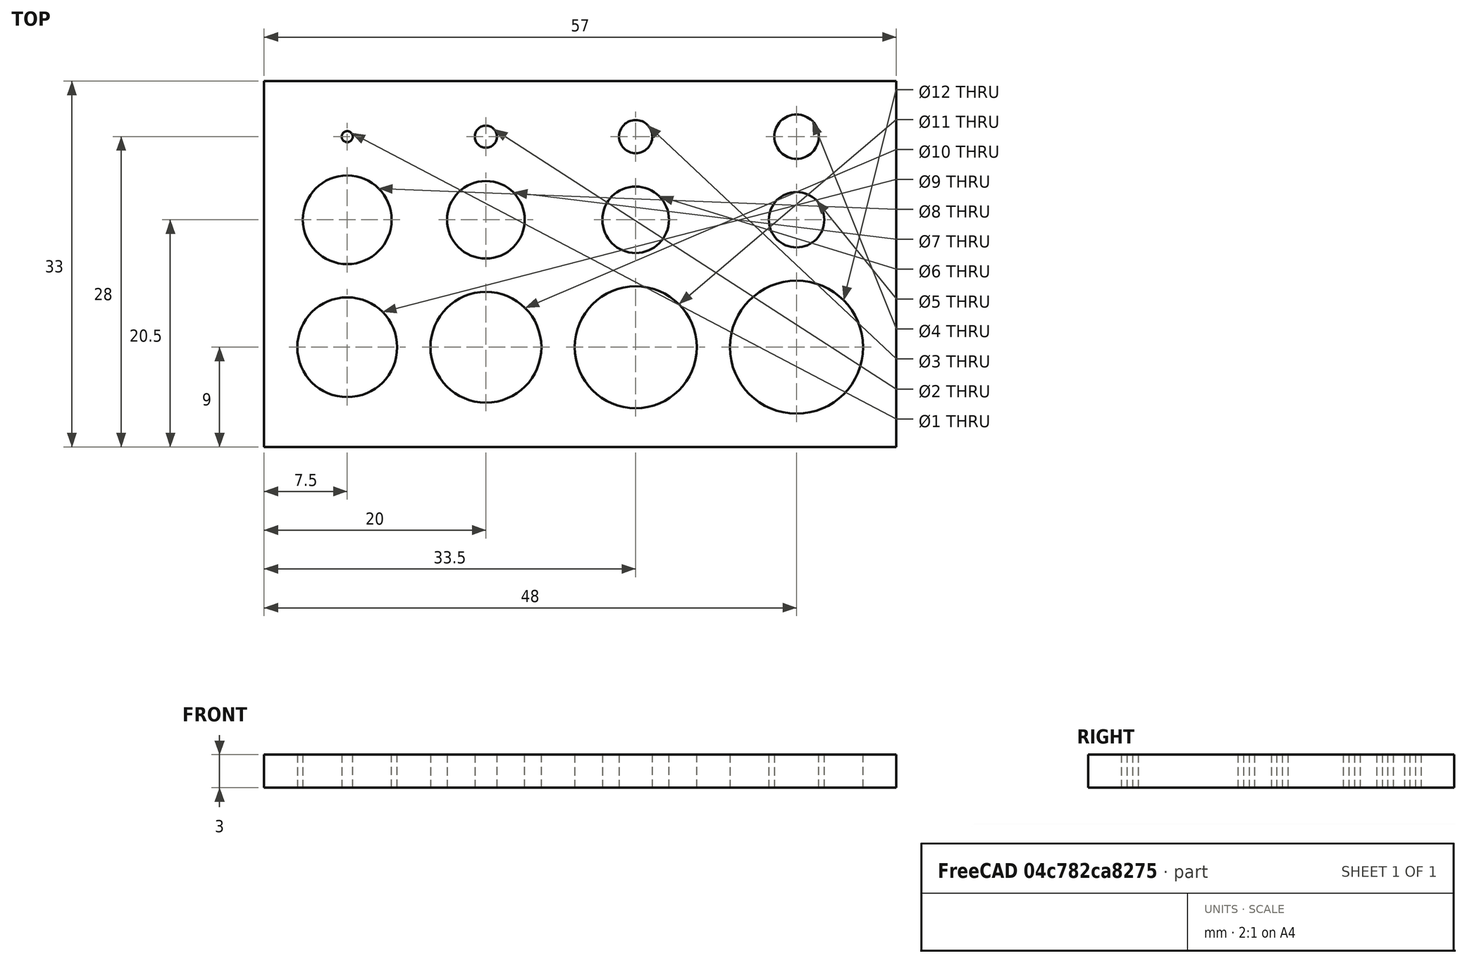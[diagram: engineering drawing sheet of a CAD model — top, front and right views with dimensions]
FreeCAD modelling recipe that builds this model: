
FCSTD DOCUMENT  (FreeCAD 0.14R3700 (Git))
Label: HolePattern
License: CC-BY 3.0
LicenseURL: http://creativecommons.org/licenses/by/3.0/
objects: Sketcher::SketchObject×1, PartDesign::Pad×1
note: 3 computed .brp shape members not serialized (recipe doc carries the construction recipe); baked Part::Feature solids carry a one-line shape summary decoded from their .brp

FEATURE [Sketcher::SketchObject] Sketch
  sketch-geometry (35):
    g0: LineSegment StartX=0 StartY=0 StartZ=0 EndX=57 EndY=0 EndZ=0
    g1: LineSegment StartX=57 StartY=0 StartZ=0 EndX=57 EndY=33 EndZ=0
    g2: LineSegment StartX=57 StartY=33 StartZ=0 EndX=0 EndY=33 EndZ=0
    g3: LineSegment StartX=0 StartY=33 StartZ=0 EndX=0 EndY=0 EndZ=0
    g4: LineSegment [constr] StartX=0 StartY=33 StartZ=0 EndX=0 EndY=28 EndZ=0
    g5: LineSegment [constr] StartX=0 StartY=28 StartZ=0 EndX=7.5 EndY=28 EndZ=0
    g6: LineSegment [constr] StartX=7.5 StartY=28 StartZ=0 EndX=20 EndY=28 EndZ=0
    g7: LineSegment [constr] StartX=20 StartY=28 StartZ=0 EndX=33.5 EndY=28 EndZ=0
    g8: LineSegment [constr] StartX=33.5 StartY=28 StartZ=0 EndX=48 EndY=28 EndZ=0
    g9: LineSegment [constr] StartX=48 StartY=28 StartZ=0 EndX=57 EndY=28 EndZ=0
    g10: LineSegment [constr] StartX=57 StartY=28 StartZ=0 EndX=57 EndY=20.5 EndZ=0
    g11: LineSegment [constr] StartX=57 StartY=20.5 StartZ=0 EndX=48 EndY=20.5 EndZ=0
    g12: LineSegment [constr] StartX=48 StartY=20.5 StartZ=0 EndX=33.5 EndY=20.5 EndZ=0
    g13: LineSegment [constr] StartX=33.5 StartY=20.5 StartZ=0 EndX=20 EndY=20.5 EndZ=0
    g14: LineSegment [constr] StartX=20 StartY=20.5 StartZ=0 EndX=7.5 EndY=20.5 EndZ=0
    g15: LineSegment [constr] StartX=7.5 StartY=20.5 StartZ=0 EndX=0 EndY=20.5 EndZ=0
    g16: LineSegment [constr] StartX=0 StartY=20.5 StartZ=0 EndX=0 EndY=9 EndZ=0
    g17: LineSegment [constr] StartX=0 StartY=9 StartZ=0 EndX=7.5 EndY=9 EndZ=0
    g18: LineSegment [constr] StartX=7.5 StartY=9 StartZ=0 EndX=20 EndY=9 EndZ=0
    g19: LineSegment [constr] StartX=20 StartY=9 StartZ=0 EndX=33.5 EndY=9 EndZ=0
    g20: LineSegment [constr] StartX=33.5 StartY=9 StartZ=0 EndX=48 EndY=9 EndZ=0
    g21: LineSegment [constr] StartX=48 StartY=9 StartZ=0 EndX=57 EndY=9 EndZ=0
    g22: LineSegment [constr] StartX=57 StartY=9 StartZ=0 EndX=57 EndY=0 EndZ=0
    g23: Circle CenterX=7.5 CenterY=28 CenterZ=0 NormalX=0 NormalY=0 NormalZ=1 Radius=0.5
    g24: Circle CenterX=20 CenterY=28 CenterZ=0 NormalX=0 NormalY=0 NormalZ=1 Radius=1
    g25: Circle CenterX=33.5 CenterY=28 CenterZ=0 NormalX=0 NormalY=0 NormalZ=1 Radius=1.5
    g26: Circle CenterX=48 CenterY=28 CenterZ=0 NormalX=0 NormalY=0 NormalZ=1 Radius=2
    g27: Circle CenterX=7.5 CenterY=20.5 CenterZ=0 NormalX=0 NormalY=0 NormalZ=1 Radius=4
    g28: Circle CenterX=20 CenterY=20.5 CenterZ=0 NormalX=0 NormalY=0 NormalZ=1 Radius=3.5
    g29: Circle CenterX=33.5 CenterY=20.5 CenterZ=0 NormalX=0 NormalY=0 NormalZ=1 Radius=3
    g30: Circle CenterX=48 CenterY=20.5 CenterZ=0 NormalX=0 NormalY=0 NormalZ=1 Radius=2.5
    g31: Circle CenterX=7.5 CenterY=9 CenterZ=0 NormalX=0 NormalY=0 NormalZ=1 Radius=4.5
    g32: Circle CenterX=20 CenterY=9 CenterZ=0 NormalX=0 NormalY=0 NormalZ=1 Radius=5
    g33: Circle CenterX=33.5 CenterY=9 CenterZ=0 NormalX=0 NormalY=0 NormalZ=1 Radius=5.5
    g34: Circle CenterX=48 CenterY=9 CenterZ=0 NormalX=0 NormalY=0 NormalZ=1 Radius=6
  constraints (91):
    c: Coincident(g0,g1)
    c: Coincident(g1,g2)
    c: Coincident(g2,g3)
    c: Coincident(g3,g0)
    c: Horizontal(g0)
    c: Horizontal(g2)
    c: Vertical(g1)
    c: Vertical(g3)
    c: Coincident(g0,g-1)
    c: Coincident(g2,g4)
    c: Coincident(g4,g5)
    c: Horizontal(g5)
    c: Coincident(g5,g6)
    c: Horizontal(g6)
    c: Coincident(g6,g7)
    c: Horizontal(g7)
    c: Coincident(g7,g8)
    c: Horizontal(g8)
    c: Coincident(g8,g9)
    c: PointOnObject(g9,g1)
    c: Horizontal(g9)
    c: Coincident(g9,g10)
    c: Coincident(g10,g11)
    c: Horizontal(g11)
    c: Coincident(g11,g12)
    c: Horizontal(g12)
    c: Coincident(g12,g13)
    c: Horizontal(g13)
    c: Coincident(g13,g14)
    c: Coincident(g14,g15)
    c: Coincident(g15,g16)
    c: Coincident(g16,g17)
    c: Horizontal(g17)
    c: Coincident(g17,g18)
    c: Horizontal(g18)
    c: Coincident(g18,g19)
    c: Coincident(g19,g20)
    c: Horizontal(g20)
    c: Coincident(g20,g21)
    c: PointOnObject(g21,g1)
    c: Horizontal(g21)
    c: Coincident(g21,g22)
    c: Horizontal(g14)
    c: Horizontal(g15)
    c: Horizontal(g19)
    c: Coincident(g22,g0)
    c: PointOnObject(g4,g3)
    c: PointOnObject(g10,g1)
    c: Coincident(g23,g5)
    c: Coincident(g24,g6)
    c: Coincident(g25,g7)
    c: Coincident(g26,g8)
    c: Coincident(g27,g14)
    c: Coincident(g28,g13)
    c: Coincident(g29,g12)
    c: Coincident(g30,g11)
    c: Coincident(g31,g17)
    c: Coincident(g32,g18)
    c: Coincident(g33,g19)
    c: Coincident(g34,g20)
    c: Radius(g34) = 6
    c: Radius(g33) = 5.5
    c: Radius(g32) = 5
    c: Radius(g31) = 4.5
    c: Radius(g30) = 2.5
    c: Radius(g29) = 3
    c: Radius(g28) = 3.5
    c: Radius(g27) = 4
    c: Radius(g26) = 2
    c: Radius(g25) = 1.5
    c: Radius(g24) = 1
    c: Radius(g23) = 0.5
    c: Distance(g21,g0) = 9
    c: Distance(g10,g21) = 11.5
    c: Distance(g9,g10) = 7.5
    c: Equal(g5,g15)
    c: Equal(g15,g17)
    c: DistanceX(g17) = 7.5
    c: PointOnObject(g16,g3)
    c: Equal(g6,g14)
    c: Equal(g14,g18)
    c: DistanceX(g18) = 12.5
    c: Equal(g7,g19)
    c: Equal(g19,g13)
    c: DistanceX(g19) = 13.5
    c: PointOnObject(g15,g3)
    c: DistanceX(g20) = 14.5
    c: DistanceX(g21) = 9
    c: Distance(g1,g9) = 5
    c: Equal(g8,g12)
    c: Equal(g12,g20)
FEATURE [PartDesign::Pad] Pad
  Length = 3
  Length2 = 100
  Sketch = -> Sketch
  Type = 0
